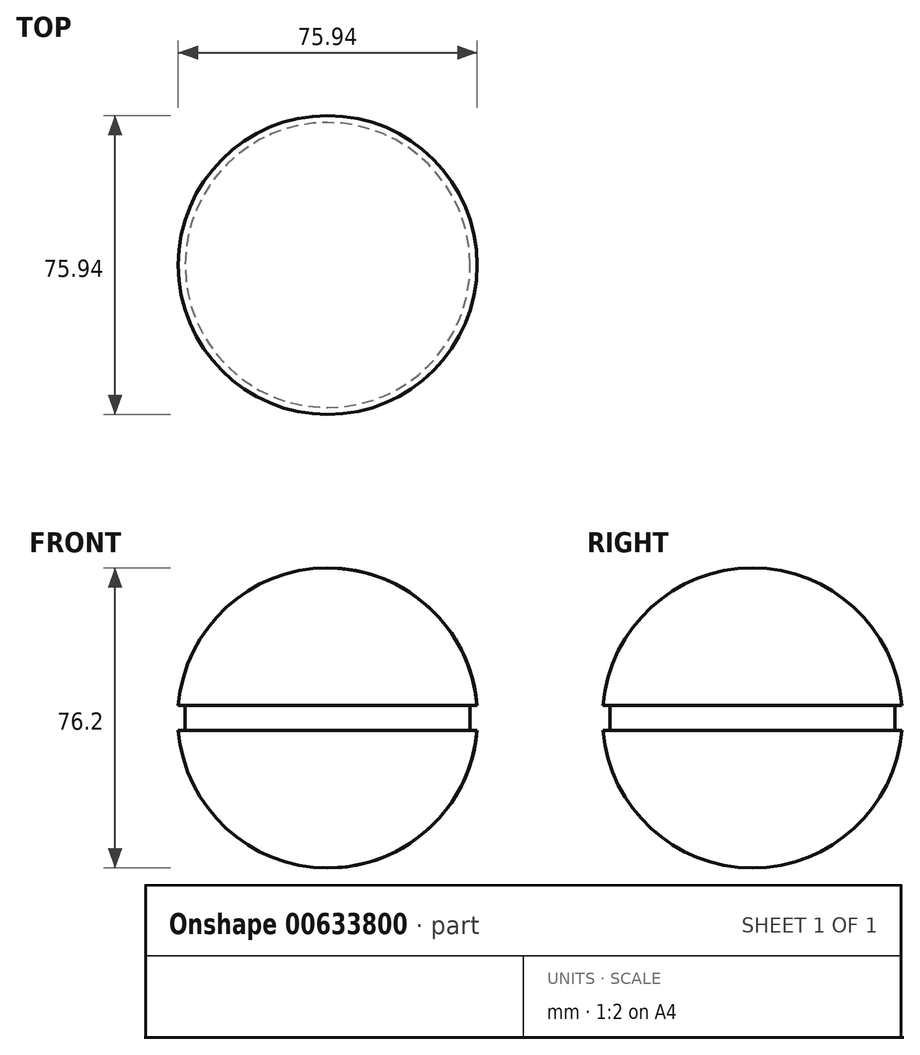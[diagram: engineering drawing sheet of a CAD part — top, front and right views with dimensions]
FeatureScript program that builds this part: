
annotation { "Feature Type Name" : "Feature", "Feature Type Description" : "" }
export const myFeature = defineFeature(function(context is Context, id is Id, definition is map)
    precondition{}
    {
        {
            var Q0;
            Q0=qCreatedBy(makeId("Top.planeOp"),FACE);
            var sketch = newSketch(context, id + "F0", { "sketchPlane" : qUnion([Q0])});
            skCircle(sketch, "E0", {"center": v(0, 0) * mm, "radius": 38.1 * mm});
            skSolve(sketch);
        }
        {
            var Q0;
            Q0=makeQuery(id+"F0.imprint","IMPRINT",FACE,{"disambiguationData":[TD([[makeQuery(id+"F0.imprint","IMPRINT",EDGE,{"derivedFrom":sQuery(id+"F0.wireOp",EDGE,"E0")}),1.0]])]});
            extrude(context, id + "F1", {"entities" : qUnion([Q0]), "endBound" : BoundingType.SYMMETRIC, "depth" : 76.2 * mm, "offsetDistance" : 25.4 * mm});
        }
        {
            var Q0;
            Q0=makeQuery(id+"F1.opExtrude","CAP_FACE",FACE,{"disambiguationData":[OSD([sQuery(id+"F0.wireOp",EDGE,"E0")])],"isStart":false});
            var Q1;
            Q1=makeQuery(id+"F1.opExtrude","CAP_EDGE",EDGE,{"disambiguationData":[OSD([sQuery(id+"F0.wireOp",EDGE,"E0")])],"isStart":true});
            fillet(context, id + "F2", {"entities" : qUnion([Q0, Q1]), "radius" : 38.1 * mm, "tangentPropagation" : true, "allowEdgeOverflow" : false});
        }
        {
            var Q0;
            Q0=qCreatedBy(makeId("Top.planeOp"),FACE);
            var sketch = newSketch(context, id + "F3", { "sketchPlane" : qUnion([Q0])});
            skCircle(sketch, "E1", {"center": v(0, 0) * mm, "radius": 38.1 * mm});
            skSolve(sketch);
        }
        {
            var Q0;
            Q0 = qSketchRegion(id + "F3", true);
            extrude(context, id + "F4", {"entities" : qUnion([Q0]), "operationType" : NewBodyOperationType.REMOVE, "endBound" : BoundingType.SYMMETRIC, "depth" : 6.35 * mm, "offsetDistance" : 25.4 * mm});
        }
        {
            var Q0;
            Q0=qCreatedBy(makeId("Top.planeOp"),FACE);
            var sketch = newSketch(context, id + "F5", { "sketchPlane" : qUnion([Q0])});
            skCircle(sketch, "E2", {"center": v(0, 0) * mm, "radius": 36.2 * mm});
            skSolve(sketch);
        }
        {
            var Q0;
            Q0 = qSketchRegion(id + "F5", true);
            extrude(context, id + "F6", {"entities" : qUnion([Q0]), "endBound" : BoundingType.SYMMETRIC, "depth" : 6.35 * mm, "offsetDistance" : 25.4 * mm});
        }
    });
